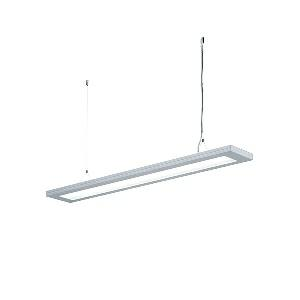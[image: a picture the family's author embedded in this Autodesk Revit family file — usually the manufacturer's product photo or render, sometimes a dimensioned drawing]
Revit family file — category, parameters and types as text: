
# Revit family: lavigo_-_dpp_9000_840_d_g2_00800466_22b8
name_source: partatom
category: Lighting Fixtures
units: mm (PartAtom-declared; Revit-internal decimal feet)

## family parameters
Cut with Voids When Loaded = No
Host = Face
Light Source = No
Part Type = Normal
Room Calculation Point = No
Round Connector Dimension = Use Diameter
Shared = No

## types (1)
- LAVIGO - DPP 9000/840/D/G2 (1 x LED, 9350 lm, 4000K)
    Apparent Load = 65 VA
    Approval mark = CE
    CIE Flux Codes = 60 87 97 19 100
    Color Rendering = 80-89
    Color Temperature = 4000K
    Control Gear = Electronic ballast
    Default Elevation = 1800 mm
    Description = DPP 9000/840/D/G2|Suspended luminaire|light source: LED|connected load: 220-240V, 50/60Hz|Power consumption: approx. 65 W|standby: approx. 0,50|luminous flux: 9350 lm|luminous efficacy: 143 lm/W|light distribution: Direct/indirect|direct ratio: approx. 19 %|colour temperature: Cold white, ca. 4000 K|color rendering index (CRI): >= 80|chromaticity tolerance:  3 SDCM|System of protection: IP 20|technology: Continuously dimmable|luminaire body|material: Steel/plastic|surface: Powder coatet|colour: Silver metallic|lamp cover: Polycarbonate (PC), Clear|mains lead: 1.00 m With free stranded wires|Fastening: Steel cable 0.3 - 0.7 m|decorative contrast side parts: Flint grey|glare control: Prism aperture|luminance(L65): <= 2800 cd/m|unified glare rating(4H 8H): <=  16|special features: Canopy colour (pure white), Cradle to Cradle Certified TM, DALI - dimming via digital rotary dimmer, DALI Load 2x, Direct light component with edge light and light-guide technology for homogenous light exit, Integration into DALI light management systems, Flicker-free, TouchDIM - dimming via standard switch|
    Frequency = 50 Hz
    Height = 36 mm
    Lamp = 1 x LED
    Lamp Light Flux = 9350 lm
    Lamp count = 1
    Length = 1245 mm
    Luminous efficacy = 144 lm/W
    Manufacturer = Waldmann
    ModVariant = No
    Model = 00800466
    Mounting Place = Ceiling
    Mounting Type = Pendant
    Number of Poles = 1
    OnlyDefault = Yes
    Power Factor = 1
    Product Name = LAVIGO - DPP 9000/840/D/G2
    Product group = Suspended luminaire
    ProductGroupID = 9
    Protection Class = Protection class I
    Protection Degree = IP 20
    RLX_Detail_Level = 1
    RLX_Emergency_Light_Flux = 0 lm
    RLX_Emergency_Type = 0
    RLX_Emergency_Type_DB = No
    RlxData = <blob elided: 25169 chars, md5=eb612277>
    Socket = socket
    Standby Power = 0 W
    System Light Flux = 9350 lm
    System Power = 65 W
    Type Comments = Product without accessories
    Type Image = 121740000-00678747.jpg
    URL = http://relux.com
    VarID = ---
    Voltage = 230 V
    Voltage Range = 220-240 V
    Weight = 0.00 kg
    Width = 200 mm  [stored 0.656168 ft]

note: [stored X ft] marks values corroborated as IEEE doubles in the binary element streams (Revit-internal decimal feet)

## geometry (parser evidence)
native form markers: Blend x4, Sweep x12
no freeform markers — native parametric forms only
